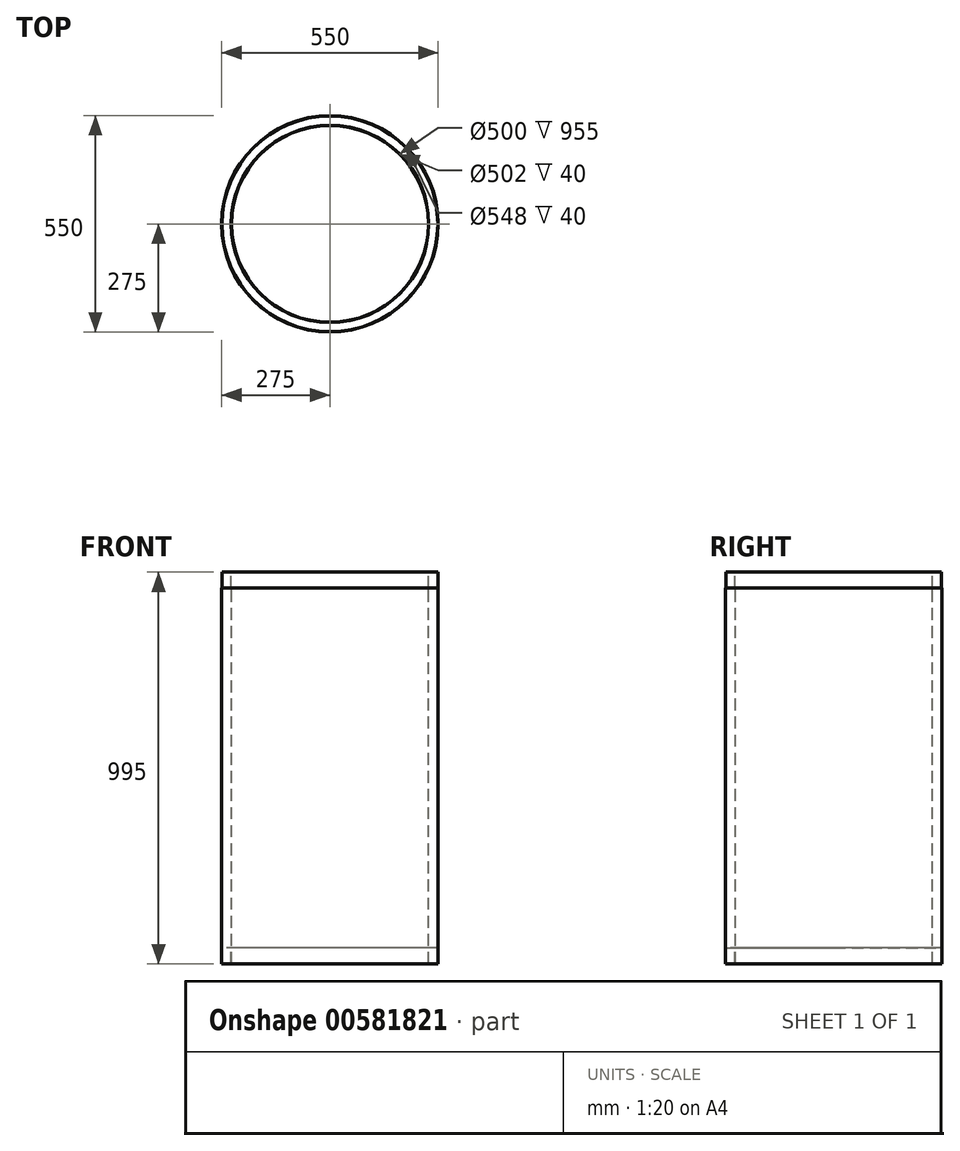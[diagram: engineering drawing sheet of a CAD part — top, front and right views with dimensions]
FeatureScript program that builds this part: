
annotation { "Feature Type Name" : "Feature", "Feature Type Description" : "" }
export const myFeature = defineFeature(function(context is Context, id is Id, definition is map)
    precondition{}
    {
        {
            var Q0;
            Q0=qCreatedBy(makeId("Front.planeOp"),FACE);
            var sketch = newSketch(context, id + "F0", { "sketchPlane" : qUnion([Q0])});
            skLineSegment(sketch, "E0", {"start": v(0, 345.75) * mm, "end": v(0, -558.03) * mm, "construction": true});
            skLineSegment(sketch, "E1", {"start": v(-250, -518.84) * mm, "end": v(-250, 436.16) * mm});
            skLineSegment(sketch, "E2", {"start": v(-250, 436.16) * mm, "end": v(-251, 436.16) * mm});
            skLineSegment(sketch, "E3", {"start": v(-251, 436.16) * mm, "end": v(-251, 476.16) * mm});
            skLineSegment(sketch, "E4", {"start": v(-251, 476.16) * mm, "end": v(-274, 476.16) * mm});
            skLineSegment(sketch, "E5", {"start": v(-274, 476.16) * mm, "end": v(-274, 436.16) * mm});
            skLineSegment(sketch, "E6", {"start": v(-274, 436.16) * mm, "end": v(-275, 436.16) * mm});
            skLineSegment(sketch, "E7", {"start": v(-275, 436.16) * mm, "end": v(-275, -518.84) * mm});
            skLineSegment(sketch, "E8", {"start": v(-275, -518.84) * mm, "end": v(-274, -518.84) * mm});
            skLineSegment(sketch, "E9", {"start": v(-274, -518.84) * mm, "end": v(-274, -478.84) * mm});
            skLineSegment(sketch, "E10", {"start": v(-274, -478.84) * mm, "end": v(-251, -478.84) * mm});
            skLineSegment(sketch, "E11", {"start": v(-251, -478.84) * mm, "end": v(-251, -518.84) * mm});
            skLineSegment(sketch, "E12", {"start": v(-251, -518.84) * mm, "end": v(-250, -518.84) * mm});
            skSolve(sketch);
        }
        {
            var Q0;
            Q0=qSketchRegion(id+"F0",true);
            var Q1;
            Q1=sQuery(id+"F0.wireOp",EDGE,"E0");
            revolve(context, id + "F1", {"entities" : qUnion([Q0]), "axis" : qUnion([Q1]), "revolveType" : RevolveType.FULL});
        }
    });
